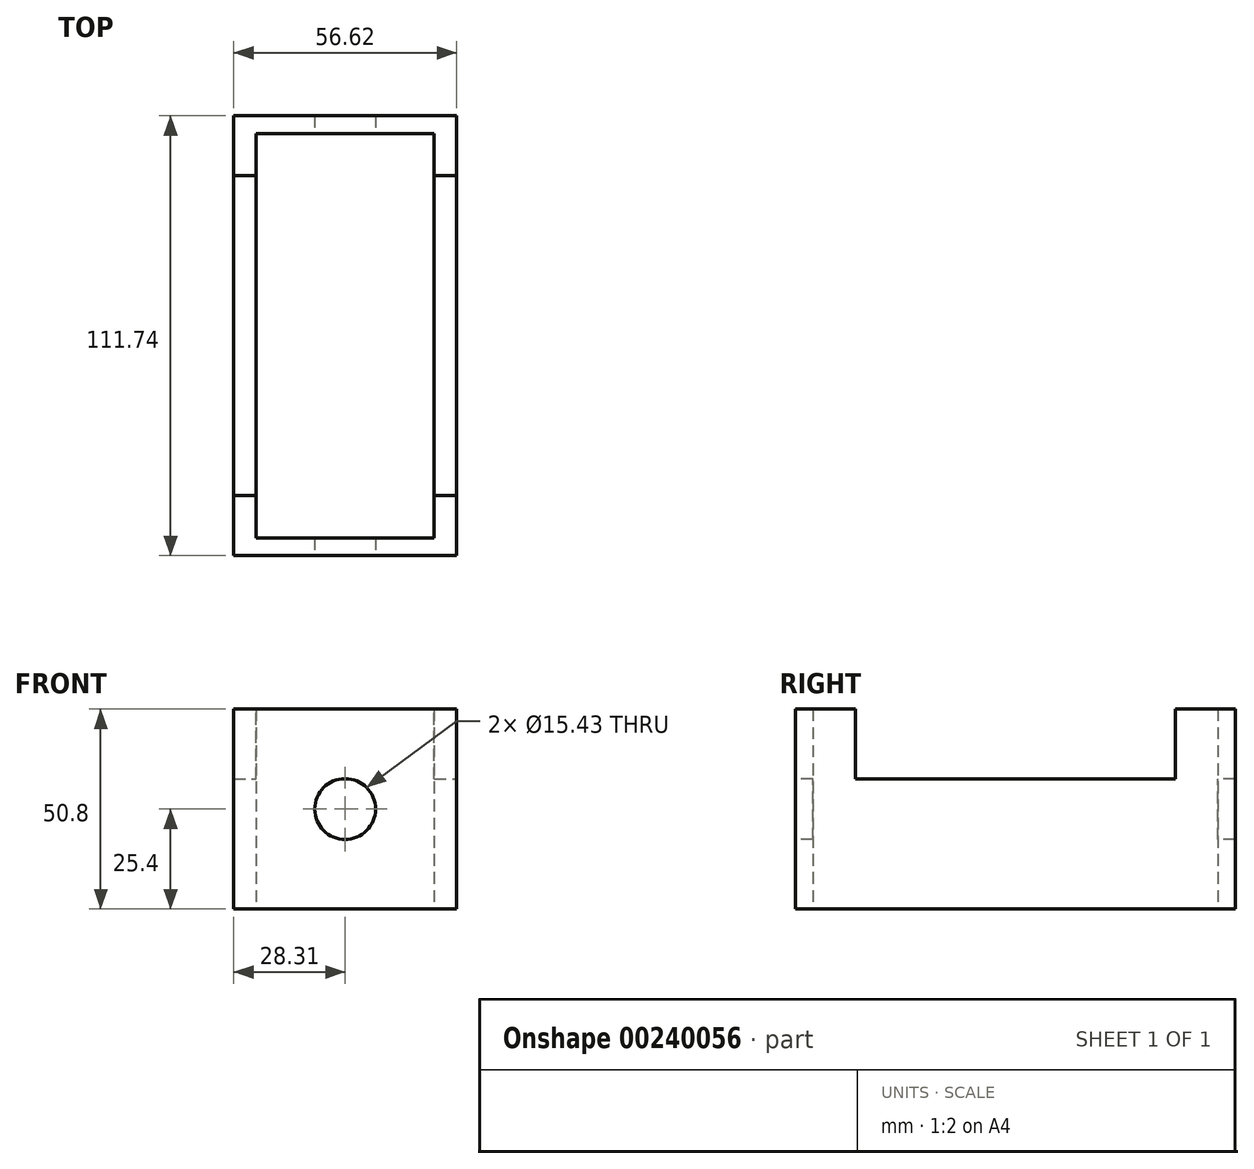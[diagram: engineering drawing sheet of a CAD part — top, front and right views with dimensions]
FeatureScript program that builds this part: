
annotation { "Feature Type Name" : "Feature", "Feature Type Description" : "" }
export const myFeature = defineFeature(function(context is Context, id is Id, definition is map)
    precondition{}
    {
        {
            var Q0;
            Q0=qCreatedBy(makeId("Top.planeOp"),FACE);
            var sketch = newSketch(context, id + "F0", { "sketchPlane" : qUnion([Q0])});
            skLineSegment(sketch, "E0.bottom", {"start": v(28.3, -55.87) * mm, "end": v(-28.3, -55.87) * mm});
            skLineSegment(sketch, "E0.top", {"start": v(28.3, 55.87) * mm, "end": v(-28.3, 55.87) * mm});
            skLineSegment(sketch, "E0.left", {"start": v(28.3, -55.87) * mm, "end": v(28.3, 55.87) * mm});
            skLineSegment(sketch, "E0.right", {"start": v(-28.3, -55.87) * mm, "end": v(-28.3, 55.87) * mm});
            skPoint(sketch, "E0.middle", {"position": v(0, 0) * mm});
            skLineSegment(sketch, "E1.bottom", {"start": v(22.65, -51.4) * mm, "end": v(-22.65, -51.4) * mm});
            skLineSegment(sketch, "E1.top", {"start": v(22.65, 51.4) * mm, "end": v(-22.65, 51.4) * mm});
            skLineSegment(sketch, "E1.left", {"start": v(22.65, -51.4) * mm, "end": v(22.65, 51.4) * mm});
            skLineSegment(sketch, "E1.right", {"start": v(-22.65, -51.4) * mm, "end": v(-22.65, 51.4) * mm});
            skSolve(sketch);
        }
        {
            var Q0;
            Q0=makeQuery(id+"F0.imprint","IMPRINT",FACE,{"disambiguationData":[TD([[makeQuery(id+"F0.imprint","IMPRINT",EDGE,{"derivedFrom":sQuery(id+"F0.wireOp",EDGE,"E0.bottom")}),-1.0]])]});
            extrude(context, id + "F1", {"entities" : qUnion([Q0]), "depth" : 50.8 * mm});
        }
        {
            var Q0;
            Q0=makeQuery(id+"F1.opExtrude","SWEPT_FACE",FACE,{"disambiguationData":[OSD([sQuery(id+"F0.wireOp",EDGE,"E0.left")])]});
            var sketch = newSketch(context, id + "F2", { "sketchPlane" : qUnion([Q0])});
            skLineSegment(sketch, "E2", {"start": v(0, 0) * mm, "end": v(0, 50.8) * mm, "construction": true});
            skPoint(sketch, "E2.endSnap0", {"position": v(0, 0) * mm});
            skLineSegment(sketch, "E3", {"start": v(0, 50.8) * mm, "end": v(-40.64, 50.8) * mm});
            skLineSegment(sketch, "E4.MirrorCS", {"start": v(0, 50.8) * mm, "end": v(40.64, 50.8) * mm});
            skLineSegment(sketch, "E5", {"start": v(-40.64, 50.8) * mm, "end": v(-40.64, 33.02) * mm});
            skLineSegment(sketch, "E6", {"start": v(-40.64, 33.02) * mm, "end": v(40.64, 33.02) * mm});
            skLineSegment(sketch, "E7", {"start": v(40.64, 33.02) * mm, "end": v(40.64, 50.8) * mm});
            skSolve(sketch);
        }
        {
            var Q0;
            Q0=makeQuery(id+"F2.imprint","IMPRINT",FACE,{"disambiguationData":[TD([[makeQuery(id+"F2.imprint","IMPRINT",EDGE,{"derivedFrom":sQuery(id+"F2.wireOp",EDGE,"E3")}),-1.0]])]});
            extrude(context, id + "F3", {"entities" : qUnion([Q0]), "operationType" : NewBodyOperationType.REMOVE, "oppositeDirection" : true, "depth" : 76.2 * mm});
        }
        {
            var Q0;
            Q0=makeQuery(id+"F1.opExtrude","SWEPT_FACE",FACE,{"disambiguationData":[OSD([sQuery(id+"F0.wireOp",EDGE,"E0.bottom")])]});
            var sketch = newSketch(context, id + "F4", { "sketchPlane" : qUnion([Q0])});
            skPoint(sketch, "E8.endSnap0", {"position": v(0, 0) * mm});
            skLineSegment(sketch, "E9", {"start": v(0, 0) * mm, "end": v(0, 25.4) * mm, "construction": true});
            skCircle(sketch, "E10", {"center": v(0, 25.4) * mm, "radius": 7.72 * mm});
            skSolve(sketch);
        }
        {
            var Q0;
            Q0=makeQuery(id+"F4.imprint","IMPRINT",FACE,{"disambiguationData":[TD([[makeQuery(id+"F4.imprint","IMPRINT",EDGE,{"derivedFrom":sQuery(id+"F4.wireOp",EDGE,"E10")}),1.0]])]});
            extrude(context, id + "F5", {"entities" : qUnion([Q0]), "operationType" : NewBodyOperationType.REMOVE, "oppositeDirection" : true, "depth" : 127 * mm});
        }
    });
